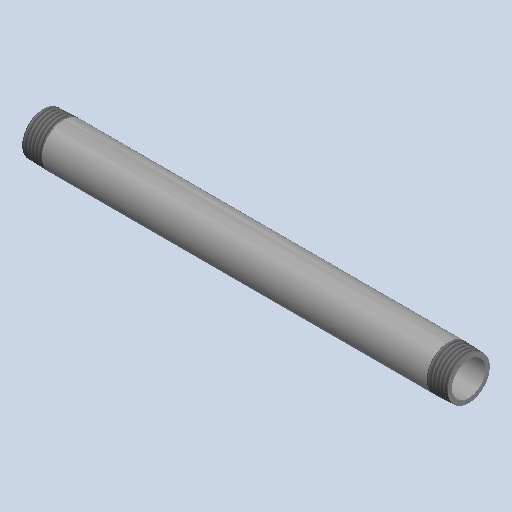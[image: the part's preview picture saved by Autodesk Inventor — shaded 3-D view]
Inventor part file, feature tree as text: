
AUTODESK INVENTOR PART (.ipt)
format: ipt  version: 2025 (Build 290162000, 162)  size: 173,056 bytes
history: native  units: mm (DEFAULTED — no unit token found)
features: other x8, revolve x1
ambient origin geometry x8: Origin, YZ Plane, XZ Plane, XY Plane, X Axis, Y Axis, Z Axis, Center Point
bodies: Solid1 (feature_tree)
feature tree (9):
  revolve  "Revolution1"  [1 undecoded]
  other  "Work Axis1"
  other  "Work Point5"
  other  "Work Axis2"
  other  "Work Point6"
  other  "Work Axis3"
  other  "Work Axis4"
  other  "Work Point7"
  other  "Work Point8"
note: 1 required parameter value undecoded (feature->parameter linkage not recoverable at this tier; creation-order binding heuristic only, values carry confidence <= 0.55)
